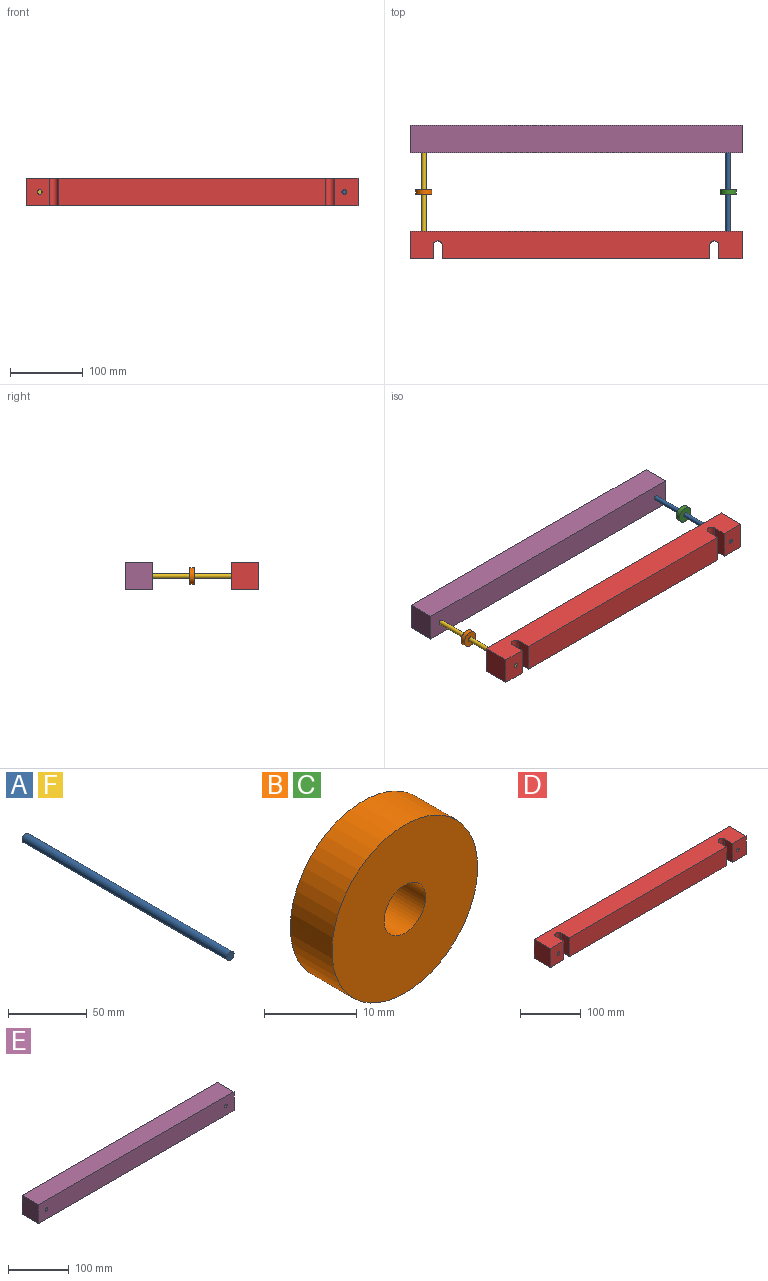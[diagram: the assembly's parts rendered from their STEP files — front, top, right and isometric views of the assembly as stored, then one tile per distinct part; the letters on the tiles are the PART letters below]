
ASSEMBLY  parts=6 mates=6
PART A: 3 faces, bbox 6.4x184.2x6.4 mm
  f0: cylinder r=3.17mm len=184.15mm, axis (0,1,0), area 3673.6mm2, adj f1,f2
  f1: plane 6.35x6.35mm, normal (0,-1,0), area 31.7mm2, adj f0
  f2: plane 6.35x6.35mm, normal (0,1,0), area 31.7mm2, adj f0
PART B: 4 faces, bbox 22.2x6.4x22.2 mm
  f0: cylinder r=11.11mm len=22.23mm, axis (0,1,0), area 443.4mm2, adj f1,f2
  f1: plane 22.23x22.23mm, normal (0,-1,0), area 356.3mm2, adj f0,f3
  f2: plane 22.23x22.23mm, normal (0,1,0), area 356.3mm2, adj f0,f3
  f3: cylinder r=3.17mm len=6.35mm, axis (0,-1,0), area 126.7mm2, adj f1,f2
PART C: same geometry as B
PART D: 16 faces, bbox 457.2x38.1x38.1 mm
  f0: plane 38.1x31.79mm, normal (0,-1,0), area 1179.5mm2, adj f2,f3,f7,f8,f15
  f1: plane 368.38x38.1mm, normal (0,-1,0), area 14035.2mm2, adj f2,f3,f12,f13
  f2: plane 457.2x38.1mm, normal (0,0,1), area 16829.5mm2, adj f0,f1,f4,f5,f6,f7,f10,f11
  f3: plane 457.2x38.1mm, normal (0,0,-1), area 16829.5mm2, adj f0,f1,f4,f5,f6,f7,f10,f11
  f4: plane 38.1x31.79mm, normal (0,-1,0), area 1179.5mm2, adj f2,f3,f6,f9,f10
  f5: plane 457.2x38.1mm, normal (0,1,0), area 17356mm2, adj f2,f3,f6,f7,f8,f9
  f6: plane 38.1x38.1mm, normal (1,0,0), area 1451.6mm2, adj f2,f3,f4,f5
  f7: plane 38.1x38.1mm, normal (-1,0,0), area 1451.6mm2, adj f0,f2,f3,f5
  f8: cylinder r=3.17mm len=38.1mm, axis (0,-1,0), area 760.1mm2, adj f0,f5
  f9: cylinder r=3.17mm len=38.1mm, axis (0,-1,0), area 760.1mm2, adj f4,f5
  f10: plane 38.1x19.05mm, normal (-1,0,0), area 725.8mm2, adj f2,f3,f4,f11
  f11: cylinder r=6.35mm len=38.1mm, axis (0,0,1), area 706.6mm2, adj f2,f3,f10,f12
  f12: plane 38.1x19.05mm, normal (1,0,0), area 725.8mm2, adj f1,f2,f3,f11
  f13: plane 38.1x19.05mm, normal (-1,0,0), area 725.8mm2, adj f1,f2,f3,f14
  f14: cylinder r=6.35mm len=38.1mm, axis (0,0,1), area 706.6mm2, adj f2,f3,f13,f15
  f15: plane 38.1x19.05mm, normal (1,0,0), area 725.8mm2, adj f0,f2,f3,f14
PART E: 8 faces, bbox 457.2x38.1x38.1 mm
  f0: plane 457.2x38.1mm, normal (0,-1,0), area 17356mm2, adj f2,f3,f4,f5,f6,f7
  f1: plane 457.2x38.1mm, normal (0,1,0), area 17356mm2, adj f2,f3,f4,f5,f6,f7
  f2: plane 38.1x38.1mm, normal (1,0,0), area 1451.6mm2, adj f0,f1,f4,f5
  f3: plane 38.1x38.1mm, normal (-1,0,0), area 1451.6mm2, adj f0,f1,f4,f5
  f4: plane 457.2x38.1mm, normal (0,0,1), area 17419.3mm2, adj f0,f1,f2,f3
  f5: plane 457.2x38.1mm, normal (0,0,-1), area 17419.3mm2, adj f0,f1,f2,f3
  f6: cylinder r=3.17mm len=38.1mm, axis (0,-1,0), area 760.1mm2, adj f0,f1
  f7: cylinder r=3.17mm len=38.1mm, axis (0,-1,0), area 760.1mm2, adj f0,f1
PART F: same geometry as A
PLACE A t=(209.55,0,19.05)mm
PLACE B t=(-209.55,-88.9,19.05)mm
PLACE C t=(209.55,-88.9,19.05)mm
PLACE D t=(0,-165.1,0)mm
PLACE E t=(0,-19.05,0)mm
PLACE F t=(-209.55,0,19.05)mm
MATE fastened A.f0 <-> E.f7  axis (0,1,0) through (209.55,0,19.05)mm
MATE fastened A.f0 <-> D.f9  axis (0,-1,0) through (209.55,-184.15,19.05)mm
MATE fastened F.f0 <-> B.f0  axis (0,1,0) through (-209.55,-92.08,19.05)mm
MATE fastened A.f0 <-> C.f3  axis (0,1,0) through (209.55,-92.07,19.05)mm
MATE fastened F.f0 <-> D.f8  axis (0,-1,0) through (-209.55,-184.15,19.05)mm
MATE fastened E.f6 <-> F.f0  axis (0,1,0) through (-209.55,0,19.05)mm
